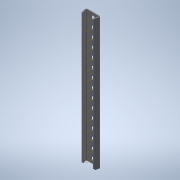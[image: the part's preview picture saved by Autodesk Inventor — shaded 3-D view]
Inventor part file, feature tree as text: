
AUTODESK INVENTOR PART (.ipt)
format: ipt  version: 2020 (Build 240168000, 168)  size: 443,904 bytes
history: native  units: in
note: dims shown in document units (in); Inventor stores cm internally (conversion verified against a paired STEP export)
features: other x18, plane x2, boolean_combine x1, extrude x1, pattern_linear x1, split x1, imported_body x1, sketch x1
ambient origin geometry x8: Origin, YZ Plane, XZ Plane, XY Plane, X Axis, Y Axis, Z Axis, Center Point
bodies: Body1 (feature_tree)
feature tree (26):
  boolean_combine  "Combine1"
  other  "Linear Slide"
  other  "Work Axis1"
  extrude  "Extrusion1"  TaperAngle=0.0deg  [1 undecoded]
  pattern_linear  "Rectangular Pattern1"  Spacing1=0.0in  [1 undecoded]
  plane  "Work Plane3"
  plane  "Work Plane4"
  split  "Split1"
  imported_body  "Base1"
  other  "Work Point1"
  other  "Work Axis2"
  sketch  "Sketch1"  dims[d0=5.9055in d2=0.5in d4=0.0in d5=0.0in d6=0.0in d9=-11.0in d10=0.0in]
  other  "Work Axis46"
  other  "Work Axis47"
  other  "Work Axis48"
  other  "Work Axis49"
  other  "Work Axis50"
  other  "Work Axis51"
  other  "Work Axis52"
  other  "Work Axis53"
  other  "Work Axis54"
  other  "Work Axis55"
  other  "Work Axis56"
  other  "Work Axis57"
  other  "Work Axis69"
  other  "bottom plane"
note: 2 required parameter values undecoded (feature->parameter linkage not recoverable at this tier; creation-order binding heuristic only, values carry confidence <= 0.55)
